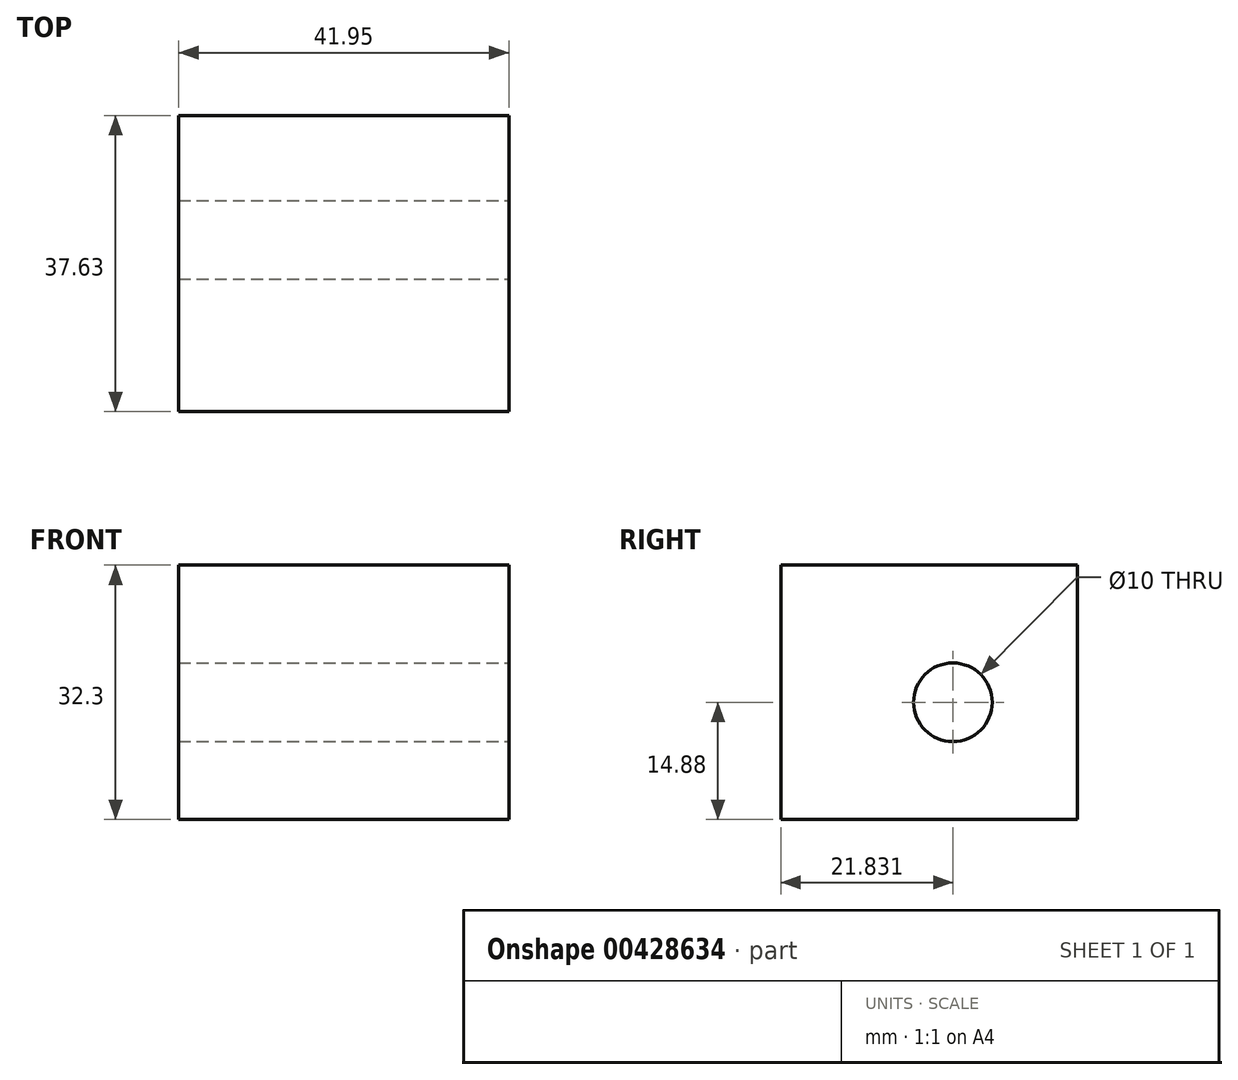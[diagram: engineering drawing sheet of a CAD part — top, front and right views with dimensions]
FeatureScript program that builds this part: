
annotation { "Feature Type Name" : "Feature", "Feature Type Description" : "" }
export const myFeature = defineFeature(function(context is Context, id is Id, definition is map)
    precondition{}
    {
        {
            var Q0;
            Q0=qCreatedBy(makeId("Top.planeOp"),FACE);
            var sketch = newSketch(context, id + "F0", { "sketchPlane" : qUnion([Q0])});
            skLineSegment(sketch, "E0.bottom", {"start": v(0, 0) * mm, "end": v(41.95, 0) * mm});
            skLineSegment(sketch, "E0.top", {"start": v(0, -37.63) * mm, "end": v(41.95, -37.63) * mm});
            skLineSegment(sketch, "E0.left", {"start": v(0, 0) * mm, "end": v(0, -37.63) * mm});
            skLineSegment(sketch, "E0.right", {"start": v(41.95, 0) * mm, "end": v(41.95, -37.63) * mm});
            skSolve(sketch);
        }
        {
            var Q0;
            Q0=makeQuery(id+"F0.imprint","IMPRINT",FACE,{"disambiguationData":[TD([[makeQuery(id+"F0.imprint","IMPRINT",EDGE,{"derivedFrom":sQuery(id+"F0.wireOp",EDGE,"E0.bottom")}),-1.0]])]});
            extrude(context, id + "F1", {"entities" : qUnion([Q0]), "depth" : 32.3 * mm});
        }
        {
            var Q0;
            Q0=makeQuery(id+"F1.opExtrude","SWEPT_FACE",FACE,{"disambiguationData":[OSD([sQuery(id+"F0.wireOp",EDGE,"E0.right")])]});
            var sketch = newSketch(context, id + "F2", { "sketchPlane" : qUnion([Q0])});
            skCircle(sketch, "E1", {"center": v(-15.8, 14.88) * mm, "radius": 5 * mm});
            skSolve(sketch);
        }
        {
            var Q0;
            Q0=makeQuery(id+"F2.imprint","IMPRINT",FACE,{"disambiguationData":[TD([[makeQuery(id+"F2.imprint","IMPRINT",EDGE,{"derivedFrom":sQuery(id+"F2.wireOp",EDGE,"E1")}),1.0]])]});
            extrude(context, id + "F3", {"entities" : qUnion([Q0]), "operationType" : NewBodyOperationType.REMOVE, "endBound" : BoundingType.THROUGH_ALL, "oppositeDirection" : true, "depth" : 25 * mm});
        }
    });
